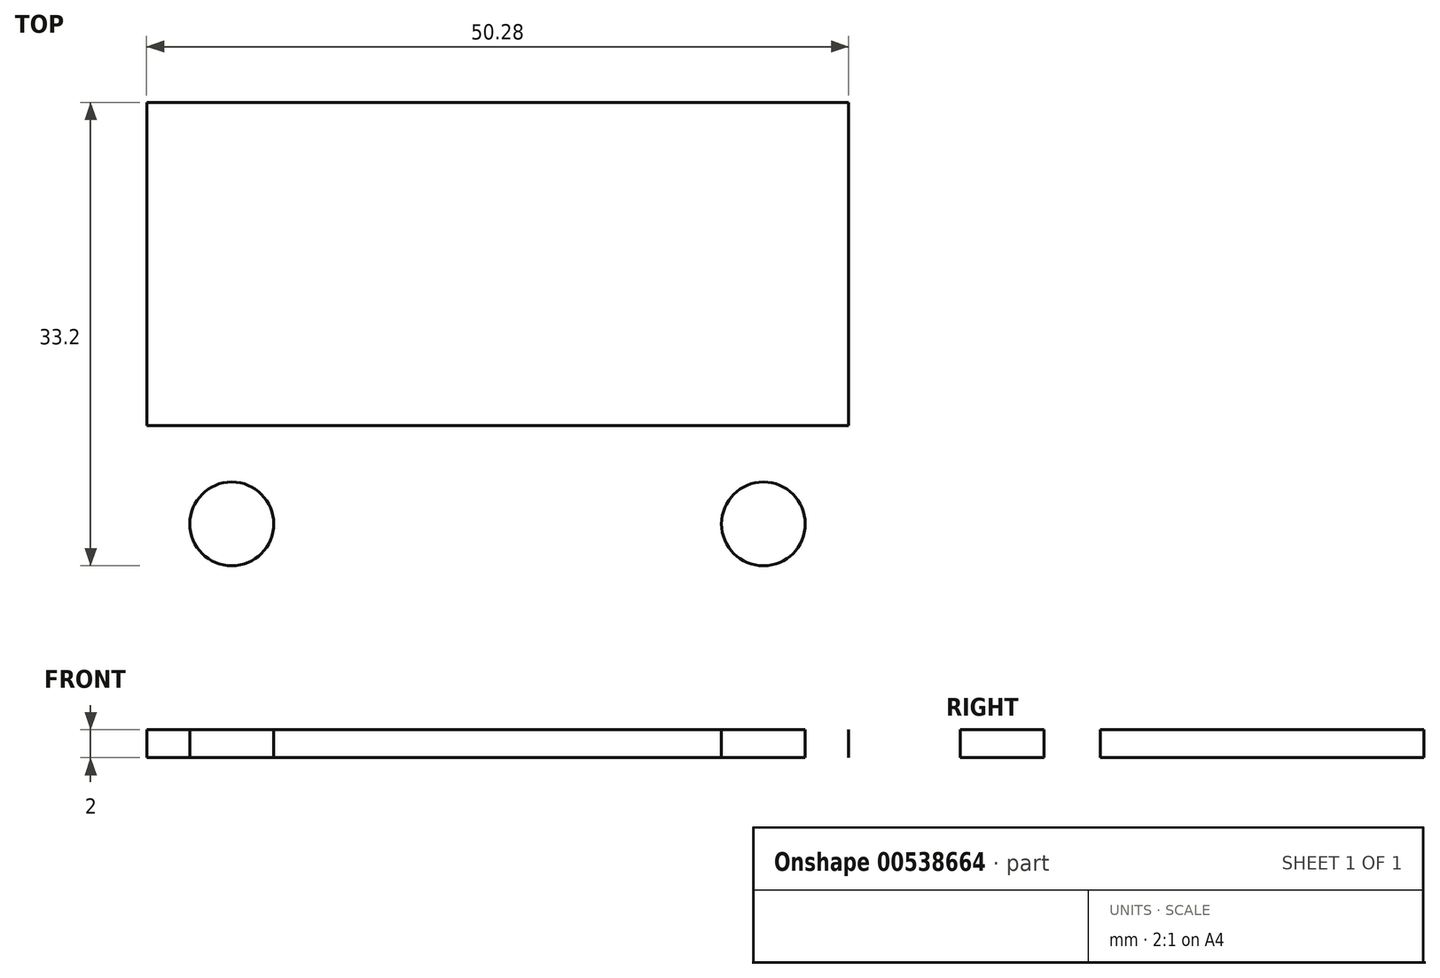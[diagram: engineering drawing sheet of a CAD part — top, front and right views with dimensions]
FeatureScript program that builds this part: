
annotation { "Feature Type Name" : "Feature", "Feature Type Description" : "" }
export const myFeature = defineFeature(function(context is Context, id is Id, definition is map)
    precondition{}
    {
        {
            var Q0;
            Q0=qCreatedBy(makeId("Top.planeOp"),FACE);
            var sketch = newSketch(context, id + "F0", { "sketchPlane" : qUnion([Q0])});
            skLineSegment(sketch, "E0.bottom", {"start": v(25.14, 0) * mm, "end": v(-25.14, 0) * mm});
            skLineSegment(sketch, "E0.top", {"start": v(25.14, -23.17) * mm, "end": v(-25.13, -23.17) * mm});
            skLineSegment(sketch, "E0.left", {"start": v(25.14, 0) * mm, "end": v(25.14, -23.17) * mm});
            skLineSegment(sketch, "E0.right", {"start": v(-25.14, 0) * mm, "end": v(-25.14, -23.17) * mm});
            skPoint(sketch, "E0.middle", {"position": v(0, -11.58) * mm});
            skLineSegment(sketch, "E1", {"start": v(-19.04, -30.2) * mm, "end": v(19.04, -30.2) * mm, "construction": true});
            skPoint(sketch, "E2", {"position": v(0, -30.2) * mm});
            skPoint(sketch, "E2.positionSnap0", {"position": v(0, -30.2) * mm});
            skCircle(sketch, "E3", {"center": v(-19.04, -30.2) * mm, "radius": 3 * mm});
            skCircle(sketch, "E4", {"center": v(19.04, -30.2) * mm, "radius": 3 * mm});
            skSolve(sketch);
        }
        {
            var Q0;
            Q0 = qSketchRegion(id + "F0", true);
            extrude(context, id + "F1", {"entities" : qUnion([Q0]), "depth" : 2 * mm, "offsetDistance" : 25 * mm});
        }
    });
